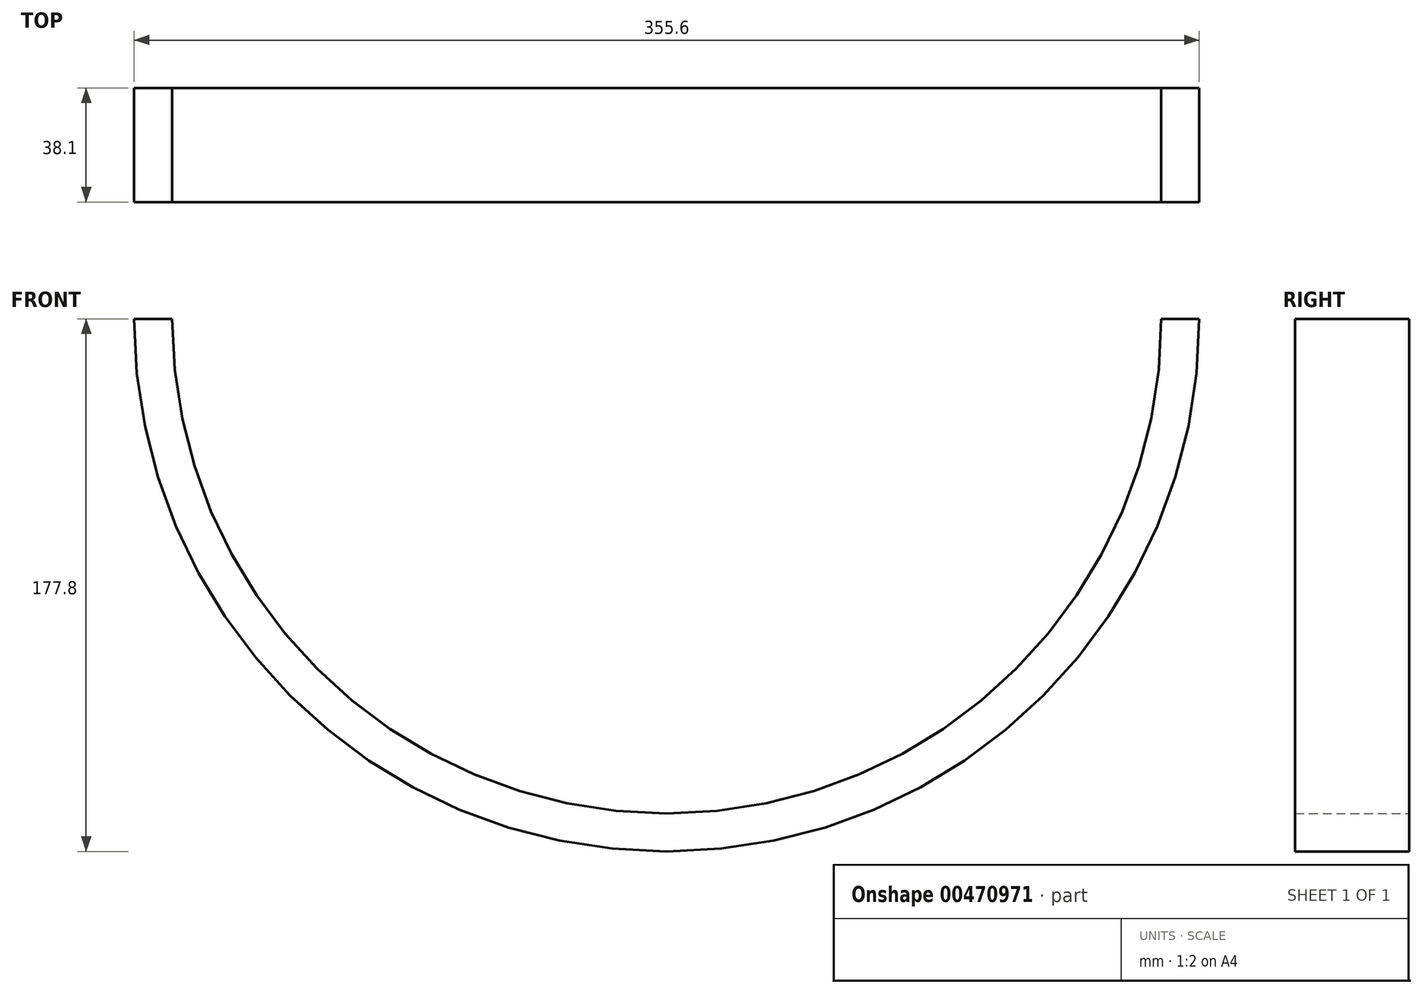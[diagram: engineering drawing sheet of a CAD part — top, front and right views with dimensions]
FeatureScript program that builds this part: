
annotation { "Feature Type Name" : "Feature", "Feature Type Description" : "" }
export const myFeature = defineFeature(function(context is Context, id is Id, definition is map)
    precondition{}
    {
        {
            var Q0;
            Q0=qCreatedBy(makeId("Front.planeOp"),FACE);
            var sketch = newSketch(context, id + "F0", { "sketchPlane" : qUnion([Q0])});
            skCircle(sketch, "E0", {"center": v(0, 0) * mm, "radius": 177.8 * mm});
            skCircle(sketch, "E1", {"center": v(0, 0) * mm, "radius": 165.1 * mm});
            skLineSegment(sketch, "E2", {"start": v(-177.8, 0) * mm, "end": v(177.8, 0) * mm});
            skSolve(sketch);
        }
        {
            var Q0;
            {var subQ0=sQuery(id+"F0.wireOp",EDGE,"E2");var subQ1=sQuery(id+"F0.wireOp",EDGE,"E0");var subQ2=makeQuery(id+"F0.imprint","INTERSECT",VERTEX,{"disambiguationData":[OD(0.0)],"derivedFrom":[subQ1,subQ0]});Q0=makeQuery(id+"F0.imprint","IMPRINT",FACE,{"disambiguationData":[TD([[makeQuery(id+"F0.imprint","IMPRINT",EDGE,{"disambiguationData":[TD([[subQ2,1.0]])],"derivedFrom":subQ1}),1.0]])]});}
            extrude(context, id + "F1", {"entities" : qUnion([Q0]), "depth" : 38.1 * mm, "offsetDistance" : 25.4 * mm});
        }
    });
